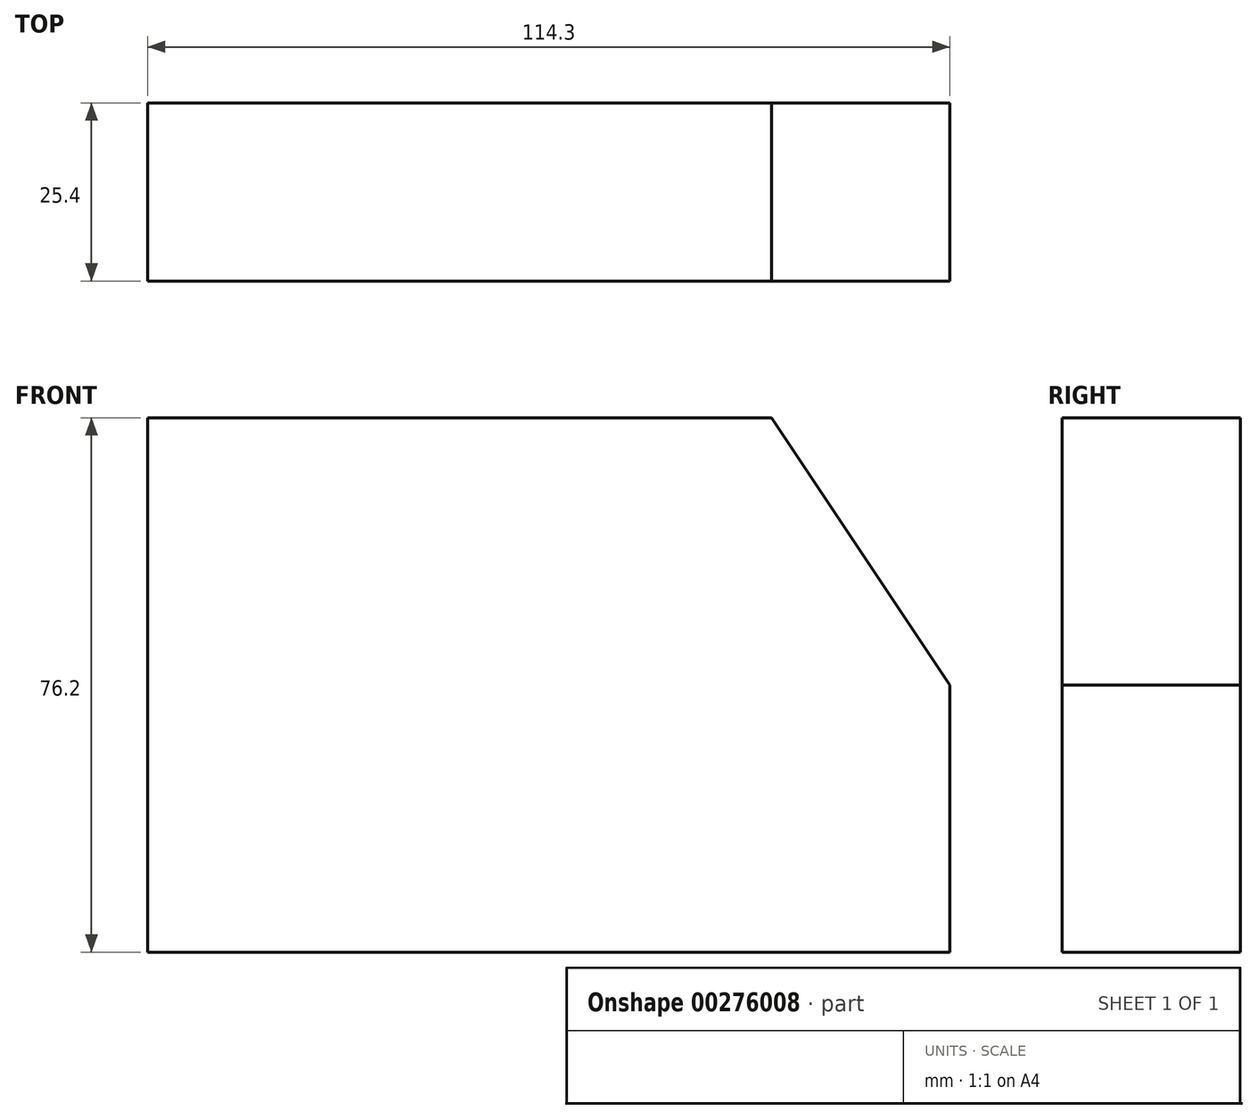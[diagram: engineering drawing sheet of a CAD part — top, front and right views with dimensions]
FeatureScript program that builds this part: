
annotation { "Feature Type Name" : "Feature", "Feature Type Description" : "" }
export const myFeature = defineFeature(function(context is Context, id is Id, definition is map)
    precondition{}
    {
        {
            var Q0;
            Q0=qCreatedBy(makeId("Front.planeOp"),FACE);
            var sketch = newSketch(context, id + "F0", { "sketchPlane" : qUnion([Q0])});
            skLineSegment(sketch, "E0.bottom", {"start": v(0, 0) * mm, "end": v(114.3, 0) * mm});
            skLineSegment(sketch, "E0.top", {"start": v(0, 76.2) * mm, "end": v(88.9, 76.2) * mm});
            skLineSegment(sketch, "E0.left", {"start": v(0, 0) * mm, "end": v(0, 76.2) * mm});
            skLineSegment(sketch, "E0.right", {"start": v(114.3, 0) * mm, "end": v(114.3, 38.1) * mm});
            skLineSegment(sketch, "E1", {"start": v(88.9, 76.2) * mm, "end": v(114.3, 38.1) * mm});
            skPoint(sketch, "E2.orphan", {"position": v(114.3, 76.2) * mm});
            skSolve(sketch);
        }
        {
            var Q0;
            Q0 = qSketchRegion(id + "F0", true);
            extrude(context, id + "F1", {"entities" : qUnion([Q0]), "depth" : 25.4 * mm});
        }
    });
